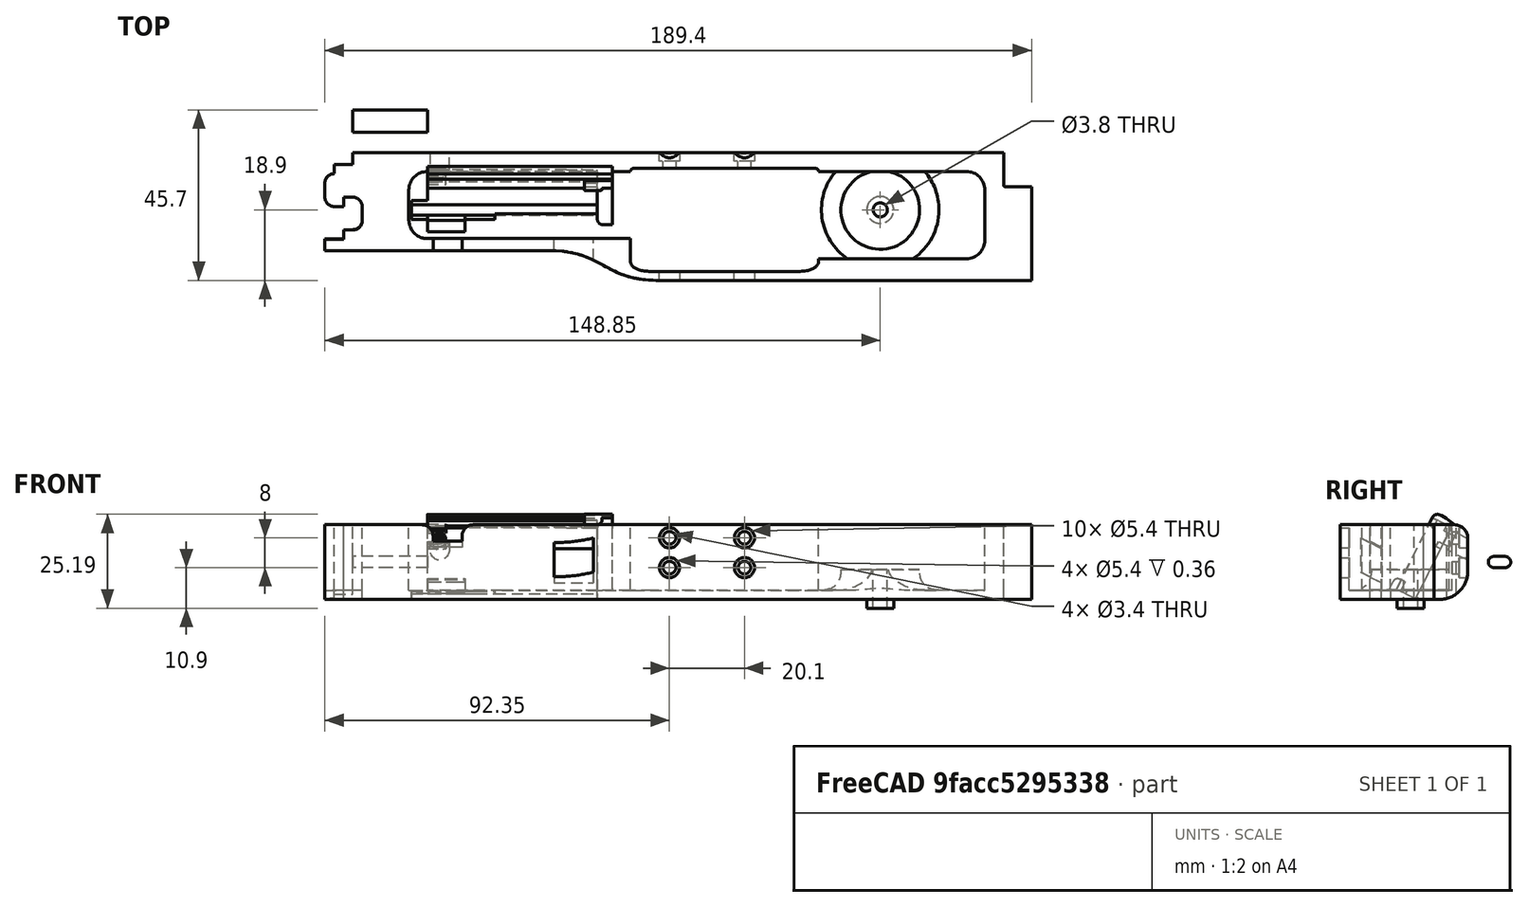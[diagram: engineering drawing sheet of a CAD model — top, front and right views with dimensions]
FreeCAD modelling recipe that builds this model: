
FCSTD DOCUMENT  (FreeCAD 0.19R0.19.2)
Label: v0_994
License: All rights reserved
LicenseURL: http://en.wikipedia.org/wiki/All_rights_reserved
objects: Sketcher::SketchObject×37, Part::Extrusion×31, Part::MultiFuse×17, Part::Cut×14, Part::Fillet×13, Part::Box×12, App::MeasureDistance×4, Part::Cylinder×4, Part::Revolution×1, Mesh::Feature×1
note: 129 computed .brp shape members not serialized (recipe doc carries the construction recipe); baked Part::Feature solids carry a one-line shape summary decoded from their .brp

FEATURE [Sketcher::SketchObject] Sketch
  FullyConstrained = true
  sketch-geometry (36):
    g0: LineSegment StartX=0 StartY=0 StartZ=0 EndX=154.4 EndY=0 EndZ=0
    g1: LineSegment StartX=154.4 StartY=0 StartZ=0 EndX=154.4 EndY=-7.6 EndZ=0
    g2: LineSegment StartX=32.5209 StartY=-26.2 StartZ=0 EndX=-7.5 EndY=-26.2 EndZ=0
    g3-g7: Circle x5 (B-spline internal-alignment scaffolding for g8; pole/knot coordinates omitted)
    g8: BSplineCurve PolesCount=5 KnotsCount=3 Degree=3 IsPeriodic=0
    g9: GeomPoint X=61.85 Y=-33.8 Z=0
    g10: GeomPoint X=47.185 Y=-29.9 Z=0
    g11: GeomPoint X=32.5209 Y=-26.2 Z=0
    g12: Circle CenterX=121.35 CenterY=-14.3 CenterZ=0 NormalX=0 NormalY=0 NormalZ=1 AngleXU=0 Radius=3.25
    g13: LineSegment StartX=-7.5 StartY=-26.2 StartZ=0 EndX=-27.5 EndY=-26.2 EndZ=0
    g14: LineSegment StartX=-20 StartY=0 StartZ=0 EndX=0 EndY=0 EndZ=0
    g15: LineSegment StartX=-25 StartY=-3.1 StartZ=0 EndX=-20 EndY=-3.1 EndZ=0
    g16: LineSegment StartX=-25 StartY=-3.1 StartZ=0 EndX=-25 EndY=-5.6 EndZ=0
    g17: LineSegment StartX=-27.5 StartY=-8.1 StartZ=0 EndX=-27.5 EndY=-11.85 EndZ=0
    g18: ArcOfCircle CenterX=-25 CenterY=-8.1 CenterZ=0 NormalX=0 NormalY=0 NormalZ=1 AngleXU=0 Radius=2.5 StartAngle=1.5708 EndAngle=3.14159
    g19: LineSegment StartX=-25 StartY=-14.35 StartZ=0 EndX=-22.5 EndY=-14.35 EndZ=0
    g20: ArcOfCircle CenterX=-25 CenterY=-11.85 CenterZ=0 NormalX=0 NormalY=0 NormalZ=1 AngleXU=0 Radius=2.5 StartAngle=3.14159 EndAngle=4.71239
    g21: LineSegment StartX=-22.5 StartY=-14.35 StartZ=0 EndX=-22.5 EndY=-11.85 EndZ=0
    g22: LineSegment StartX=-22.5 StartY=-11.85 StartZ=0 EndX=-20 EndY=-11.85 EndZ=0
    g23: ArcOfCircle CenterX=-20 CenterY=-14.35 CenterZ=0 NormalX=0 NormalY=0 NormalZ=1 AngleXU=0 Radius=2.5 StartAngle=8e-16 EndAngle=1.5708
    g24: LineSegment StartX=-17.5 StartY=-14.35 StartZ=0 EndX=-17.5 EndY=-18.1 EndZ=0
    g25: ArcOfCircle CenterX=-20 CenterY=-18.1 CenterZ=0 NormalX=0 NormalY=0 NormalZ=1 AngleXU=0 Radius=2.5 StartAngle=4.71239 EndAngle=6.28319
    g26: LineSegment StartX=-22.5 StartY=-20.6 StartZ=0 EndX=-20 EndY=-20.6 EndZ=0
    g27: LineSegment StartX=-22.5 StartY=-20.6 StartZ=0 EndX=-22.5 EndY=-23.1 EndZ=0
    g28: LineSegment StartX=-27.5 StartY=-23.1 StartZ=0 EndX=-22.5 EndY=-23.1 EndZ=0
    g29: LineSegment StartX=-20 StartY=-3.1 StartZ=0 EndX=-20 EndY=0 EndZ=0
    g30: LineSegment StartX=-27.5 StartY=-23.1 StartZ=0 EndX=-27.5 EndY=-26.2 EndZ=0
    g31: LineSegment StartX=154.4 StartY=-7.6 StartZ=0 EndX=154.4 EndY=-8.6 EndZ=0
    g32: ArcOfCircle CenterX=154.9 CenterY=-8.6 CenterZ=0 NormalX=0 NormalY=0 NormalZ=1 AngleXU=0 Radius=0.5 StartAngle=3.14159 EndAngle=4.71239
    g33: LineSegment StartX=154.9 StartY=-9.1 StartZ=0 EndX=161.9 EndY=-9.1 EndZ=0
    g34: LineSegment StartX=161.9 StartY=-9.1 StartZ=0 EndX=161.9 EndY=-33.8 EndZ=0
    g35: LineSegment StartX=161.9 StartY=-33.8 StartZ=0 EndX=61.85 EndY=-33.8 EndZ=0
  constraints (72):
    c: PointOnObject(g0,g-2)
    c: Horizontal(g0)
    c: Distance(g0) = 154.4
    c: DistanceY(g-1,g0) = 0
    c: Vertical(g1)
    c: Distance(g1) = 7.6
    c: Coincident(g1,g0)
    c: Horizontal(g2)
    c: Block(g2)
    c: Weight(g3) = 1
    c: Coincident(g8,g2)
    c: InternalAlignment(g3-g7 -> g8) x5
    c: InternalAlignment(g9,g8)
    c: InternalAlignment(g10,g8)
    c: InternalAlignment(g11,g8)
    c: Block(g12)
    c: Coincident(g13,g2)
    c: Horizontal(g13)
    c: Distance(g13) = 20
    c: Horizontal(g14)
    c: Distance(g14) = 20
    c: Coincident(g14,g0)
    c: Horizontal(g15)
    c: Vertical(g16)
    c: Coincident(g16,g15)
    c: Vertical(g17)
    c: Coincident(g18,g16)
    c: Block(g18)
    c: Coincident(g17,g18)
    c: Horizontal(g19)
    c: Coincident(g20,g17)
    c: Block(g20)
    c: Block(g19)
    c: Vertical(g21)
    c: Coincident(g21,g19)
    c: Horizontal(g22)
    c: Coincident(g22,g21)
    c: Coincident(g23,g22)
    c: Vertical(g24)
    c: Block(g23)
    c: Coincident(g24,g23)
    c: Coincident(g25,g24)
    c: Block(g25)
    c: Horizontal(g26)
    c: Coincident(g26,g25)
    c: Vertical(g27)
    c: Coincident(g27,g26)
    c: Horizontal(g28)
    c: Coincident(g28,g27)
    c: Block(g15)
    c: Block(g28)
    c: Coincident(g29,g15)
    c: Coincident(g29,g14)
    c: Vertical(g29)
    c: Coincident(g30,g28)
    c: Coincident(g30,g13)
    c: Vertical(g30)
    c: Vertical(g31)
    c: Distance(g31) = 1
    c: Coincident(g31,g1)
    c: Coincident(g32,g31)
    c: Block(g32)
    c: Coincident(g33,g32)
    c: Horizontal(g33)
    c: Coincident(g34,g33)
    c: Vertical(g34)
    c: Block(g34)
    c: Coincident(g35,g34)
    c: Horizontal(g35)
    c: Block(g35)
    c: Coincident(g8,g35)
    c: Block(g8)
FEATURE [Part::Extrusion] Extrude  label="mainBodyBaseExtrude"
  Base = -> Sketch
  Dir = (0,0,1)
  DirMode = 2
  FaceMakerClass = Part::FaceMakerBullseye
  LengthFwd = 2.4
  LengthRev = 0
  Solid = true
  Symmetric = false
FEATURE [Sketcher::SketchObject] Sketch001
  FullyConstrained = true
  sketch-geometry (75):
    g0: ArcOfCircle CenterX=144.4 CenterY=-10 CenterZ=0 NormalX=0 NormalY=0 NormalZ=1 AngleXU=0 Radius=5 StartAngle=4.345e-13 EndAngle=1.5708
    g1: LineSegment StartX=32.5209 StartY=-26.2 StartZ=0 EndX=-7.49911 EndY=-26.2 EndZ=0
    g2: LineSegment StartX=0 StartY=0 StartZ=0 EndX=154.4 EndY=0 EndZ=0
    g3-g7: Circle x5 (B-spline internal-alignment scaffolding for g8; pole/knot coordinates omitted)
    g8: BSplineCurve PolesCount=5 KnotsCount=3 Degree=3 IsPeriodic=0
    g9: GeomPoint X=61.85 Y=-33.8 Z=0
    g10: GeomPoint X=47.1857 Y=-29.9 Z=0
    g11: GeomPoint X=32.5209 Y=-26.2 Z=0
    g12: LineSegment StartX=154.4 StartY=0 StartZ=0 EndX=154.4 EndY=-7.6 EndZ=0
    g13: LineSegment StartX=20 StartY=-5 StartZ=0 EndX=54.35 EndY=-5 EndZ=0
    g14: LineSegment StartX=104.85 StartY=-5 StartZ=0 EndX=144.4 EndY=-5 EndZ=0
    g15: LineSegment StartX=54.35 StartY=-23 StartZ=0 EndX=20 EndY=-23 EndZ=0
    g16: LineSegment StartX=-27.4991 StartY=-26.2 StartZ=0 EndX=-7.49911 EndY=-26.2 EndZ=0
    g17: LineSegment StartX=-20 StartY=0 StartZ=0 EndX=0 EndY=0 EndZ=0
    g18: LineSegment StartX=-27.4991 StartY=-23.2 StartZ=0 EndX=-22.5 EndY=-23.2 EndZ=0
    g19: LineSegment StartX=-22.5 StartY=-20.7 StartZ=0 EndX=-22.5 EndY=-23.2 EndZ=0
    g20: LineSegment StartX=-22.5 StartY=-20.7 StartZ=0 EndX=-20 EndY=-20.7 EndZ=0
    g21: ArcOfCircle CenterX=-20 CenterY=-18.2 CenterZ=0 NormalX=0 NormalY=0 NormalZ=1 AngleXU=0 Radius=2.5 StartAngle=4.71239 EndAngle=6.28319
    g22: LineSegment StartX=-17.5 StartY=-14.4 StartZ=0 EndX=-17.5 EndY=-18.2 EndZ=0
    g23: ArcOfCircle CenterX=-20 CenterY=-14.4 CenterZ=0 NormalX=0 NormalY=0 NormalZ=1 AngleXU=0 Radius=2.5 StartAngle=9e-16 EndAngle=1.5708
    g24: LineSegment StartX=-22.5 StartY=-11.9 StartZ=0 EndX=-20 EndY=-11.9 EndZ=0
    g25: LineSegment StartX=-22.5 StartY=-14.4 StartZ=0 EndX=-22.5 EndY=-11.9 EndZ=0
    g26: LineSegment StartX=-25 StartY=-14.4 StartZ=0 EndX=-22.5 EndY=-14.4 EndZ=0
    g27: ArcOfCircle CenterX=-25 CenterY=-11.9 CenterZ=0 NormalX=0 NormalY=0 NormalZ=1 AngleXU=0 Radius=2.5 StartAngle=3.14159 EndAngle=4.71239
    g28: LineSegment StartX=-27.5 StartY=-8.1 StartZ=0 EndX=-27.5 EndY=-11.9 EndZ=0
    g29: ArcOfCircle CenterX=-25 CenterY=-8.1 CenterZ=0 NormalX=0 NormalY=0 NormalZ=1 AngleXU=0 Radius=2.5 StartAngle=1.5708 EndAngle=3.14159
    g30: LineSegment StartX=-25 StartY=-3.1 StartZ=0 EndX=-25 EndY=-5.6 EndZ=0
    g31: LineSegment StartX=-20 StartY=-3.1 StartZ=0 EndX=-25 EndY=-3.1 EndZ=0
    g32: LineSegment StartX=-20 StartY=0 StartZ=0 EndX=-20 EndY=-3.1 EndZ=0
    g33: LineSegment StartX=-27.4991 StartY=-26.2 StartZ=0 EndX=-27.4991 EndY=-23.2 EndZ=0
    g34: LineSegment StartX=4.09e-14 StartY=-5 StartZ=0 EndX=20 EndY=-5 EndZ=0
    g35: ArcOfCircle CenterX=7.1e-15 CenterY=-18 CenterZ=0 NormalX=0 NormalY=0 NormalZ=1 AngleXU=0 Radius=5 StartAngle=3.14159 EndAngle=4.71239
    g36: ArcOfCircle CenterX=4.26e-14 CenterY=-10 CenterZ=0 NormalX=0 NormalY=0 NormalZ=1 AngleXU=0 Radius=5 StartAngle=1.5708 EndAngle=3.14159
    g37: LineSegment StartX=-5 StartY=-18 StartZ=0 EndX=-5 EndY=-10 EndZ=0
    g38: LineSegment StartX=6.2e-15 StartY=-23 StartZ=0 EndX=20 EndY=-23 EndZ=0
    g39: LineSegment StartX=154.4 StartY=-7.6 StartZ=0 EndX=154.4 EndY=-8.6 EndZ=0
    g40: LineSegment StartX=154.9 StartY=-9.1 StartZ=0 EndX=161.9 EndY=-9.1 EndZ=0
    g41: ArcOfCircle CenterX=154.9 CenterY=-8.6 CenterZ=0 NormalX=0 NormalY=0 NormalZ=1 AngleXU=0 Radius=0.5 StartAngle=3.14159 EndAngle=4.71299
    g42: LineSegment StartX=104.85 StartY=-28.3916 StartZ=0 EndX=144.408 EndY=-28.3916 EndZ=0
    g43: LineSegment StartX=149.4 StartY=-10 StartZ=0 EndX=149.4 EndY=-23.4 EndZ=0
    g44: ArcOfCircle CenterX=144.408 CenterY=-23.4 CenterZ=0 NormalX=0 NormalY=0 NormalZ=1 AngleXU=0 Radius=4.99164 StartAngle=4.71239 EndAngle=6.28319
    g45: LineSegment StartX=104.85 StartY=-28.3916 StartZ=0 EndX=104.85 EndY=-28.7833 EndZ=0
    g46: LineSegment StartX=54.35 StartY=-28.7916 StartZ=0 EndX=54.35 EndY=-23 EndZ=0
    g47: LineSegment StartX=161.9 StartY=-33.8 StartZ=0 EndX=161.9 EndY=-9.1 EndZ=0
    g48: LineSegment StartX=61.85 StartY=-33.8 StartZ=0 EndX=161.9 EndY=-33.8 EndZ=0
    g49: Circle CenterX=54.35 CenterY=-28.7916 CenterZ=0 NormalX=0 NormalY=0 NormalZ=1 AngleXU=0 Radius=1
    g50: Circle CenterX=54.35 CenterY=-31.7916 CenterZ=0 NormalX=0 NormalY=0 NormalZ=1 AngleXU=0 Radius=1
    g51: Circle CenterX=57.35 CenterY=-31.7916 CenterZ=0 NormalX=0 NormalY=0 NormalZ=1 AngleXU=0 Radius=1
    g52: BSplineCurve PolesCount=3 KnotsCount=2 Degree=2 IsPeriodic=0
    g53: GeomPoint X=54.35 Y=-28.7916 Z=0
    g54: GeomPoint X=57.35 Y=-31.7916 Z=0
    g55: Circle CenterX=104.85 CenterY=-28.7833 CenterZ=0 NormalX=0 NormalY=0 NormalZ=1 AngleXU=0 Radius=1
    g56: Circle CenterX=104.85 CenterY=-31.7916 CenterZ=0 NormalX=0 NormalY=0 NormalZ=1 AngleXU=0 Radius=1
    g57: Circle CenterX=101.85 CenterY=-31.7916 CenterZ=0 NormalX=0 NormalY=0 NormalZ=1 AngleXU=0 Radius=1
    g58: BSplineCurve PolesCount=3 KnotsCount=2 Degree=2 IsPeriodic=0
    g59: GeomPoint X=104.85 Y=-28.7833 Z=0
    g60: GeomPoint X=101.85 Y=-31.7916 Z=0
    g61: LineSegment StartX=57.35 StartY=-31.7916 StartZ=0 EndX=101.85 EndY=-31.7916 EndZ=0
    g62: Circle CenterX=54.35 CenterY=-5 CenterZ=0 NormalX=0 NormalY=0 NormalZ=1 AngleXU=0 Radius=1
    g63: Circle CenterX=54.35 CenterY=-4 CenterZ=0 NormalX=0 NormalY=0 NormalZ=1 AngleXU=0 Radius=1
    g64: Circle CenterX=55.15 CenterY=-4 CenterZ=0 NormalX=0 NormalY=0 NormalZ=1 AngleXU=0 Radius=1
    g65: BSplineCurve PolesCount=3 KnotsCount=2 Degree=2 IsPeriodic=0
    g66: GeomPoint X=54.35 Y=-5 Z=0
    g67: GeomPoint X=55.15 Y=-4 Z=0
    g68: Circle CenterX=104.85 CenterY=-5 CenterZ=0 NormalX=0 NormalY=0 NormalZ=1 AngleXU=0 Radius=1
    g69: Circle CenterX=104.85 CenterY=-4 CenterZ=0 NormalX=0 NormalY=0 NormalZ=1 AngleXU=0 Radius=1
    g70: Circle CenterX=104.05 CenterY=-4 CenterZ=0 NormalX=0 NormalY=0 NormalZ=1 AngleXU=0 Radius=1
    g71: BSplineCurve PolesCount=3 KnotsCount=2 Degree=2 IsPeriodic=0
    g72: GeomPoint X=104.85 Y=-5 Z=0
    g73: GeomPoint X=104.05 Y=-4 Z=0
    g74: LineSegment StartX=104.05 StartY=-4 StartZ=0 EndX=55.15 EndY=-4 EndZ=0
  constraints (156):
    c: PointOnObject(g2,g-2)
    c: DistanceY(g-1,g2) = 0
    c: Block(g0)
    c: Horizontal(g1)
    c: Distance(g1) = 40.02
    c: Horizontal(g2)
    c: Block(g2)
    c: Weight(g3) = 1
    c: Equal(g3, g4-g7) x4
    c: Coincident(g8,g1)
    c: InternalAlignment(g3-g7 -> g8) x5
    c: InternalAlignment(g9,g8)
    c: InternalAlignment(g10,g8)
    c: InternalAlignment(g11,g8)
    c: Vertical(g12)
    c: Coincident(g12,g2)
    c: Distance(g12) = 7.6
    c: Block(g12)
    c: Horizontal(g13)
    c: Coincident(g14,g0)
    c: Horizontal(g14)
    c: Horizontal(g15)
    c: Horizontal(g16)
    c: Distance(g16) = 20
    c: Coincident(g1,g16)
    c: Horizontal(g17)
    c: Distance(g17) = 20
    c: Coincident(g17,g2)
    c: Horizontal(g31)
    c: Vertical(g30)
    c: Coincident(g29,g30)
    c: Vertical(g28)
    c: Block(g29)
    c: Coincident(g27,g28)
    c: Block(g27)
    c: Horizontal(g26)
    c: Coincident(g26,g27)
    c: Vertical(g25)
    c: Coincident(g25,g26)
    c: Horizontal(g24)
    c: Coincident(g23,g24)
    c: Block(g23)
    c: Vertical(g22)
    c: Coincident(g21,g22)
    c: Block(g21)
    c: Horizontal(g20)
    c: Coincident(g20,g21)
    c: Vertical(g19)
    c: Coincident(g19,g20)
    c: Horizontal(g18)
    c: Coincident(g18,g19)
    c: Coincident(g32,g17)
    c: Coincident(g32,g31)
    c: Vertical(g32)
    c: Coincident(g33,g16)
    c: Coincident(g33,g18)
    c: Vertical(g33)
    c: Block(g33)
    c: Block(g18)
    c: Block(g22)
    c: Block(g26)
    c: Block(g25)
    c: Block(g24)
    c: Block(g28)
    c: Block(g31)
    c: Block(g30)
    c: Horizontal(g34)
    c: Distance(g34) = 20
    c: Block(g35)
    c: Block(g36)
    c: Coincident(g37,g35)
    c: Coincident(g37,g36)
    c: Vertical(g37)
    c: Coincident(g38,g35)
    c: Coincident(g38,g15)
    c: Horizontal(g38)
    c: Block(g38)
    c: Block(g34)
    c: Block(g13)
    c: Vertical(g39)
    c: Distance(g39) = 1
    c: Coincident(g39,g12)
    c: Horizontal(g40)
    c: Coincident(g41,g39)
    c: Coincident(g41,g40)
    c: Block(g39)
    c: Block(g41)
    c: Horizontal(g42)
    c: Vertical(g43)
    c: Distance(g43) = 13.4
    c: Coincident(g43,g0)
    c: Block(g42)
    c: Block(g43)
    c: Coincident(g44,g43)
    c: Coincident(g44,g42)
    c: Block(g44)
    c: Distance(g15) = 34.35
    c: Coincident(g45,g42)
    c: Vertical(g45)
    c: Coincident(g46,g15)
    c: Vertical(g46)
    c: Coincident(g47,g40)
    c: Vertical(g47)
    c: Block(g47)
    c: Coincident(g48,g47)
    c: Horizontal(g48)
    c: Block(g48)
    c: Coincident(g8,g48)
    c: Block(g8)
    c: Coincident(g52,g46)
    c: Weight(g49) = 1
    c: Equal(g49,g50)
    c: Equal(g49,g51)
    c: InternalAlignment(g49,g52)
    c: InternalAlignment(g50,g52)
    c: InternalAlignment(g51,g52)
    c: InternalAlignment(g53,g52)
    c: InternalAlignment(g54,g52)
    c: Coincident(g58,g45)
    c: Weight(g55) = 1
    c: Equal(g55,g56)
    c: Equal(g55,g57)
    c: InternalAlignment(g55,g58)
    c: InternalAlignment(g56,g58)
    c: InternalAlignment(g57,g58)
    c: InternalAlignment(g59,g58)
    c: InternalAlignment(g60,g58)
    c: Block(g58)
    c: Block(g52)
    c: Coincident(g61,g52)
    c: Coincident(g61,g58)
    c: Horizontal(g61)
    c: Block(g14)
    c: Coincident(g65,g13)
    c: Weight(g62) = 1
    c: Equal(g62,g63)
    c: Equal(g62,g64)
    c: InternalAlignment(g62,g65)
    c: InternalAlignment(g63,g65)
    c: InternalAlignment(g64,g65)
    c: InternalAlignment(g66,g65)
    c: InternalAlignment(g67,g65)
    c: Block(g65)
    c: Coincident(g71,g14)
    c: Weight(g68) = 1
    c: Equal(g68,g69)
    c: Equal(g68,g70)
    c: InternalAlignment(g68,g71)
    c: InternalAlignment(g69,g71)
    c: InternalAlignment(g70,g71)
    c: InternalAlignment(g72,g71)
    c: InternalAlignment(g73,g71)
    c: Block(g71)
    c: Coincident(g74,g71)
    c: Coincident(g74,g65)
    c: Horizontal(g74)
FEATURE [Sketcher::SketchObject] Sketch005
  FullyConstrained = true
  Placement = pos=(0,0,0) rot=(1,0,0;1.5708rad)
  sketch-geometry (4):
    g0: Circle CenterX=84.95 CenterY=16.5 CenterZ=0 NormalX=0 NormalY=0 NormalZ=1 AngleXU=0 Radius=1.7
    g1: Circle CenterX=84.95 CenterY=8.5 CenterZ=0 NormalX=0 NormalY=0 NormalZ=1 AngleXU=0 Radius=1.7
    g2: Circle CenterX=64.85 CenterY=8.5 CenterZ=0 NormalX=0 NormalY=0 NormalZ=1 AngleXU=0 Radius=1.7
    g3: Circle CenterX=64.85 CenterY=16.5 CenterZ=0 NormalX=0 NormalY=0 NormalZ=1 AngleXU=0 Radius=1.7
  constraints (4):
    c: Block(g0)
    c: Block(g1)
    c: Block(g2)
    c: Block(g3)
FEATURE [Part::Extrusion] Extrude004  label="removeFromMainBodyToCreateScrewHolesForSolenoidExtrude004"
  Base = -> Sketch005
  Dir = (0,-1,1.1e-15)
  DirMode = 2
  FaceMakerClass = Part::FaceMakerBullseye
  LengthFwd = 10
  LengthRev = 0
  Solid = true
  Symmetric = false
FEATURE [Sketcher::SketchObject] Sketch004
  FullyConstrained = true
  Placement = pos=(0,0,0) rot=(1,0,0;1.5708rad)
  sketch-geometry (12):
    g0: LineSegment StartX=15.75 StartY=2.5 StartZ=0 EndX=15.75 EndY=0 EndZ=0
    g1: Circle CenterX=15.75 CenterY=2.5 CenterZ=0 NormalX=0 NormalY=0 NormalZ=1 AngleXU=0 Radius=1
    g2: Circle CenterX=10.55 CenterY=2.5 CenterZ=0 NormalX=0 NormalY=0 NormalZ=1 AngleXU=0 Radius=1
    g3: Circle CenterX=10.55 CenterY=8 CenterZ=0 NormalX=0 NormalY=0 NormalZ=1 AngleXU=0 Radius=1
    g4: BSplineCurve PolesCount=3 KnotsCount=2 Degree=2 IsPeriodic=0
    g5: GeomPoint X=15.75 Y=2.5 Z=0
    g6: GeomPoint X=10.55 Y=8 Z=0
    g7: LineSegment StartX=1.9 StartY=8 StartZ=0 EndX=10.55 EndY=8 EndZ=0
    g8: LineSegment StartX=1.9 StartY=-2.4 StartZ=0 EndX=1.9 EndY=8 EndZ=0
    g9: LineSegment StartX=3.30092 StartY=-2.4 StartZ=0 EndX=3.30092 EndY=0 EndZ=0
    g10: LineSegment StartX=15.75 StartY=0 StartZ=0 EndX=3.30092 EndY=0 EndZ=0
    g11: LineSegment StartX=3.30092 StartY=-2.4 StartZ=0 EndX=1.9 EndY=-2.4 EndZ=0
  constraints (26):
    c: Vertical(g0)
    c: Distance(g0) = 2.5
    c: Coincident(g4,g0)
    c: Weight(g1) = 1
    c: Equal(g1,g2)
    c: Equal(g1,g3)
    c: InternalAlignment(g1,g4)
    c: InternalAlignment(g2,g4)
    c: InternalAlignment(g3,g4)
    c: InternalAlignment(g5,g4)
    c: InternalAlignment(g6,g4)
    c: Block(g4)
    c: Coincident(g7,g4)
    c: Horizontal(g7)
    c: Vertical(g8)
    c: Coincident(g8,g7)
    c: Block(g8)
    c: Vertical(g9)
    c: Coincident(g10,g0)
    c: PointOnObject(g10,g-1)
    c: Horizontal(g10)
    c: Coincident(g10,g9)
    c: Block(g9)
    c: Coincident(g11,g9)
    c: Coincident(g11,g8)
    c: Horizontal(g11)
FEATURE [Sketcher::SketchObject] Sketch007
  FullyConstrained = true
  Placement = pos=(0,-14.3,2.37) rot=(-1,0,0;2.03453rad)
  sketch-geometry (6):
    g0: LineSegment StartX=0 StartY=0 StartZ=0 EndX=45.5 EndY=0 EndZ=0
    g1: LineSegment StartX=0 StartY=0 StartZ=0 EndX=0 EndY=-21.2 EndZ=0
    g2: LineSegment StartX=45.5 StartY=0 StartZ=0 EndX=49.5 EndY=0 EndZ=0
    g3: LineSegment StartX=49.5 StartY=0 StartZ=0 EndX=49.5 EndY=-21.2 EndZ=0
    g4: LineSegment StartX=49.5 StartY=-21.2 StartZ=0 EndX=0 EndY=-21.2 EndZ=0
    g5: Circle CenterX=3.25 CenterY=-18.05 CenterZ=0 NormalX=0 NormalY=0 NormalZ=1 AngleXU=0 Radius=1.6
  constraints (15):
    c: Coincident(g0,g-1)
    c: Horizontal(g0)
    c: Distance(g0) = 45.5
    c: Coincident(g1,g0)
    c: Vertical(g1)
    c: Horizontal(g2)
    c: Distance(g2) = 4
    c: Coincident(g2,g0)
    c: Coincident(g3,g2)
    c: Vertical(g3)
    c: Block(g3)
    c: Coincident(g4,g3)
    c: Horizontal(g4)
    c: Coincident(g4,g1)
    c: Block(g5)
FEATURE [Part::Extrusion] Extrude005  label="solenoidDriverHolderExtrude005"
  Base = -> Sketch007
  Dir = (0,0.894389,-0.447291)
  DirMode = 2
  FaceMakerClass = Part::FaceMakerBullseye
  LengthFwd = 10
  LengthRev = 0
  Placement = pos=(0,0,-2) rot=(0,0,1;0rad)
  Solid = true
  Symmetric = false
FEATURE [Sketcher::SketchObject] Sketch008
  FullyConstrained = false
  Placement = pos=(0,-4.3,-2.6) rot=(-1,0,0;2.03453rad)
  sketch-geometry (1):
    g0: Circle CenterX=42.25 CenterY=-3.15 CenterZ=0 NormalX=0 NormalY=0 NormalZ=1 AngleXU=0 Radius=4.5
FEATURE [Sketcher::SketchObject] Sketch009
  FullyConstrained = true
  Placement = pos=(0,-4.3,-2.6) rot=(-1,0,0;2.03453rad)
  sketch-geometry (1):
    g0: Circle CenterX=3.25 CenterY=-18.0217 CenterZ=0 NormalX=0 NormalY=0 NormalZ=1 AngleXU=0 Radius=2.8
  constraints (1):
    c: Block(g0)
FEATURE [Sketcher::SketchObject] Sketch010
  FullyConstrained = true
  Placement = pos=(0,-14.3,2.37) rot=(-1,0,0;2.03453rad)
  sketch-geometry (1):
    g0: Circle CenterX=3.25 CenterY=-18.05 CenterZ=0 NormalX=0 NormalY=0 NormalZ=1 AngleXU=0 Radius=1.6
  constraints (1):
    c: Block(g0)
FEATURE [Part::Extrusion] Extrude008  label="removeFromScrewHole3"
  Base = -> Sketch010
  Dir = (0,0.894389,-0.447291)
  DirMode = 2
  FaceMakerClass = Part::FaceMakerBullseye
  LengthFwd = -25
  LengthRev = 0
  Placement = pos=(0,4,-4) rot=(0,0,1;0rad)
  Solid = true
  Symmetric = false
FEATURE [Sketcher::SketchObject] Sketch011
  FullyConstrained = true
  Placement = pos=(0,-14.3,2.37) rot=(-1,0,0;2.03453rad)
  sketch-geometry (4):
    g0: LineSegment StartX=49.5 StartY=-21.2 StartZ=0 EndX=49.5 EndY=-22.8 EndZ=0
    g1: LineSegment StartX=49.5 StartY=-22.8 StartZ=0 EndX=0.002238 EndY=-22.8 EndZ=0
    g2: LineSegment StartX=0.002238 StartY=-21.2 StartZ=0 EndX=0.002238 EndY=-22.8 EndZ=0
    g3: LineSegment StartX=49.5 StartY=-21.2 StartZ=0 EndX=0.002238 EndY=-21.2 EndZ=0
  constraints (10):
    c: Vertical(g0)
    c: Distance(g0) = 1.6
    c: Coincident(g1,g0)
    c: Horizontal(g1)
    c: Vertical(g2)
    c: Coincident(g2,g1)
    c: Coincident(g3,g0)
    c: Coincident(g3,g2)
    c: Horizontal(g3)
    c: Block(g3)
FEATURE [Part::Extrusion] Extrude009  label="solenoidDriverTopLipFront"
  Base = -> Sketch011
  Dir = (0,0.894389,-0.447291)
  DirMode = 2
  FaceMakerClass = Part::FaceMakerBullseye
  LengthFwd = -2
  LengthRev = 0
  Placement = pos=(0,-2.9,-0.35) rot=(0,0,1;0rad)
  Solid = true
  Symmetric = false
FEATURE [Sketcher::SketchObject] Sketch012
  FullyConstrained = true
  Placement = pos=(0,-14.3,2.37) rot=(-1,0,0;2.03453rad)
  sketch-geometry (4):
    g0: LineSegment StartX=49.5 StartY=-21.2 StartZ=0 EndX=49.5 EndY=-22.8 EndZ=0
    g1: LineSegment StartX=49.5 StartY=-22.8 StartZ=0 EndX=0.002238 EndY=-22.8 EndZ=0
    g2: LineSegment StartX=0.002238 StartY=-21.2 StartZ=0 EndX=0.002238 EndY=-22.8 EndZ=0
    g3: LineSegment StartX=49.5 StartY=-21.2 StartZ=0 EndX=0.002238 EndY=-21.2 EndZ=0
  constraints (10):
    c: Vertical(g0)
    c: Distance(g0) = 1.6
    c: Coincident(g1,g0)
    c: Horizontal(g1)
    c: Vertical(g2)
    c: Coincident(g2,g1)
    c: Coincident(g3,g0)
    c: Coincident(g3,g2)
    c: Horizontal(g3)
    c: Block(g3)
FEATURE [Part::Extrusion] Extrude010  label="solenoidDriverTopLipLowerExtrude010"
  Base = -> Sketch012
  Dir = (0,0.894389,-0.447291)
  DirMode = 2
  FaceMakerClass = Part::FaceMakerBullseye
  LengthFwd = 5.05
  LengthRev = 0
  Solid = true
  Symmetric = false
FEATURE [Sketcher::SketchObject] Sketch015
  FullyConstrained = true
  Placement = pos=(0,-14.3,2.37) rot=(-1,0,0;2.03453rad)
  sketch-geometry (4):
    g0: LineSegment StartX=0 StartY=1.5 StartZ=0 EndX=0 EndY=0 EndZ=0
    g1: LineSegment StartX=0 StartY=1.5 StartZ=0 EndX=5 EndY=1.5 EndZ=0
    g2: LineSegment StartX=5 StartY=1.5 StartZ=0 EndX=5 EndY=0 EndZ=0
    g3: LineSegment StartX=0 StartY=0 StartZ=0 EndX=5 EndY=0 EndZ=0
  constraints (13):
    c: Vertical(g0)
    c: Distance(g0) = 1.5
    c: Horizontal(g1)
    c: Distance(g1) = 5
    c: Coincident(g1,g0)
    c: Vertical(g2)
    c: Distance(g2) = 1.5
    c: Coincident(g2,g1)
    c: Block(g1)
    c: Block(g2)
    c: Block(g0)
    c: Coincident(g3,g0)
    c: Coincident(g3,g2)
FEATURE [Part::Extrusion] Extrude013  label="solenoidDriverBottomLipTopExtrude012"
  Base = -> Sketch015
  Dir = (0,0.894389,-0.447291)
  DirMode = 2
  FaceMakerClass = Part::FaceMakerBullseye
  LengthFwd = -6.5
  LengthRev = 0
  Placement = pos=(0,-14.15,19.65) rot=(1,0,0;1.5708rad)
  Solid = true
  Symmetric = false
FEATURE [Sketcher::SketchObject] Sketch016
  FullyConstrained = true
  Placement = pos=(0,0,0) rot=(1,0,0;1.5708rad)
  sketch-geometry (4):
    g0: Circle CenterX=84.15 CenterY=16.5 CenterZ=0 NormalX=0 NormalY=0 NormalZ=1 AngleXU=0 Radius=2.7
    g1: Circle CenterX=64.05 CenterY=16.5 CenterZ=0 NormalX=0 NormalY=0 NormalZ=1 AngleXU=0 Radius=2.7
    g2: Circle CenterX=64.05 CenterY=8.5 CenterZ=0 NormalX=0 NormalY=0 NormalZ=1 AngleXU=0 Radius=2.7
    g3: Circle CenterX=84.15 CenterY=8.5 CenterZ=0 NormalX=0 NormalY=0 NormalZ=1 AngleXU=0 Radius=2.7
  constraints (4):
    c: Block(g0)
    c: Block(g1)
    c: Block(g3)
    c: Block(g2)
FEATURE [Part::Extrusion] Extrude014  label="removeFromMainBodyToCreateScrewHoleCounterSinks"
  Base = -> Sketch016
  Dir = (0,-1,1.1e-15)
  DirMode = 2
  FaceMakerClass = Part::FaceMakerBullseye
  LengthFwd = 1.9
  LengthRev = 0
  Placement = pos=(0.8,-0.36,0) rot=(0,0,1;0rad)
  Solid = true
  Symmetric = false
FEATURE [Part::Extrusion] Extrude015  label="removeFromScrewHole2Extrude007"
  Base = -> Sketch009
  Dir = (0,0.894389,-0.447291)
  DirMode = 2
  FaceMakerClass = Part::FaceMakerBullseye
  LengthFwd = 10
  LengthRev = 0
  Placement = pos=(0,-8,2) rot=(0,0,1;0rad)
  Solid = true
  Symmetric = false
FEATURE [Sketcher::SketchObject] Sketch017
  FullyConstrained = true
  Placement = pos=(0,-14.3,2.37) rot=(-1,0,0;2.03453rad)
  sketch-geometry (4):
    g0: LineSegment StartX=0 StartY=1.5 StartZ=0 EndX=0 EndY=0 EndZ=0
    g1: LineSegment StartX=0 StartY=1.5 StartZ=0 EndX=5 EndY=1.5 EndZ=0
    g2: LineSegment StartX=5 StartY=1.5 StartZ=0 EndX=5 EndY=0 EndZ=0
    g3: LineSegment StartX=0 StartY=0 StartZ=0 EndX=5 EndY=0 EndZ=0
  constraints (13):
    c: Vertical(g0)
    c: Distance(g0) = 1.5
    c: Horizontal(g1)
    c: Distance(g1) = 5
    c: Coincident(g1,g0)
    c: Vertical(g2)
    c: Distance(g2) = 1.5
    c: Coincident(g2,g1)
    c: Block(g1)
    c: Block(g2)
    c: Block(g0)
    c: Coincident(g3,g0)
    c: Coincident(g3,g2)
FEATURE [Part::Extrusion] Extrude016  label="solenoidDriverBottomLipTopExtrude013"
  Base = -> Sketch017
  Dir = (0,0.894389,-0.447291)
  DirMode = 2
  FaceMakerClass = Part::FaceMakerBullseye
  LengthFwd = -6.5
  LengthRev = 0
  Placement = pos=(0,-15.45,20.3) rot=(1,0,0;1.5708rad)
  Solid = true
  Symmetric = false
FEATURE [Part::Fillet] Fillet005  label="solenoidDriverBottomLipTopFillet005"
  Base = -> Extrude016
  Edges = 1 edges r=1.4: [Edge6]
FEATURE [Sketcher::SketchObject] Sketch018
  FullyConstrained = true
  Placement = pos=(38.5,-14.3,2.37) rot=(-1,0,0;2.03453rad)
  sketch-geometry (4):
    g0: LineSegment StartX=11 StartY=0 StartZ=0 EndX=11 EndY=1.5 EndZ=0
    g1: LineSegment StartX=11 StartY=0 StartZ=0 EndX=3.6 EndY=0 EndZ=0
    g2: LineSegment StartX=3.6 StartY=0 StartZ=0 EndX=3.6 EndY=1.5 EndZ=0
    g3: LineSegment StartX=11 StartY=1.5 StartZ=0 EndX=3.6 EndY=1.5 EndZ=0
  constraints (12):
    c: PointOnObject(g0,g-1)
    c: Vertical(g0)
    c: Distance(g0) = 1.5
    c: Horizontal(g1)
    c: Distance(g1) = 7.4
    c: Coincident(g1,g0)
    c: Block(g0)
    c: Coincident(g2,g1)
    c: Vertical(g2)
    c: Coincident(g3,g0)
    c: Horizontal(g3)
    c: Coincident(g2,g3)
FEATURE [Part::Extrusion] Extrude017
  Base = -> Sketch018
  Dir = (0,0.894389,-0.447291)
  DirMode = 2
  FaceMakerClass = Part::FaceMakerBullseye
  LengthFwd = 4
  LengthRev = 0
  Placement = pos=(0,-8.212,34.025) rot=(1,0,0;1.5708rad)
  Solid = true
  Symmetric = false
FEATURE [Sketcher::SketchObject] Sketch019
  FullyConstrained = true
  Placement = pos=(0,0,0) rot=(1,0,0;1.5708rad)
  sketch-geometry (4):
    g0: Circle CenterX=84.95 CenterY=8.5 CenterZ=0 NormalX=0 NormalY=0 NormalZ=1 AngleXU=0 Radius=2.7
    g1: Circle CenterX=64.85 CenterY=8.5 CenterZ=0 NormalX=0 NormalY=0 NormalZ=1 AngleXU=0 Radius=2.7
    g2: Circle CenterX=64.85 CenterY=16.5 CenterZ=0 NormalX=0 NormalY=0 NormalZ=1 AngleXU=0 Radius=2.7
    g3: Circle CenterX=84.95 CenterY=16.5 CenterZ=0 NormalX=0 NormalY=0 NormalZ=1 AngleXU=0 Radius=2.7
  constraints (4):
    c: Block(g3)
    c: Block(g2)
    c: Block(g0)
    c: Block(g1)
FEATURE [Part::Extrusion] Extrude019  label="removeSolenoidAdjusterHoles"
  Base = -> Sketch019
  Dir = (0,-1,1.1e-15)
  DirMode = 2
  FaceMakerClass = Part::FaceMakerBullseye
  LengthFwd = 6
  LengthRev = 0
  Placement = pos=(0,-30,0) rot=(0,0,1;0rad)
  Solid = true
  Symmetric = false
FEATURE [Sketcher::SketchObject] Sketch020
  FullyConstrained = true
  Placement = pos=(0,-14.3,2.37) rot=(-1,0,0;2.03453rad)
  sketch-geometry (6):
    g0: LineSegment StartX=45.5 StartY=-21.2 StartZ=0 EndX=49.5 EndY=-21.2 EndZ=0
    g1: LineSegment StartX=45.5 StartY=0 StartZ=0 EndX=49.5 EndY=0 EndZ=0
    g2: LineSegment StartX=49.5 StartY=0 StartZ=0 EndX=49.5 EndY=-21.2 EndZ=0
    g3: LineSegment StartX=4 StartY=0 StartZ=0 EndX=4 EndY=-21.2 EndZ=0
    g4: LineSegment StartX=45.5 StartY=-21.2 StartZ=0 EndX=4 EndY=-21.2 EndZ=0
    g5: LineSegment StartX=4 StartY=0 StartZ=0 EndX=45.5 EndY=0 EndZ=0
  constraints (16):
    c: Horizontal(g0)
    c: Distance(g0) = 4
    c: Horizontal(g1)
    c: Distance(g1) = 4
    c: Coincident(g2,g1)
    c: Coincident(g2,g0)
    c: Vertical(g2)
    c: Block(g2)
    c: Vertical(g3)
    c: Coincident(g4,g0)
    c: Horizontal(g4)
    c: Coincident(g4,g3)
    c: Coincident(g5,g1)
    c: Horizontal(g5)
    c: Block(g3)
    c: Block(g5)
FEATURE [Part::Box] Box  label="Cube"
  AttacherType = Attacher::AttachEngine3D
  Height = 10
  Length = 190
  Placement = pos=(-30,0,0) rot=(0,0,1;0rad)
  Width = 10
FEATURE [Part::Fillet] Fillet008
  Base = -> Box
  Edges = 1 edges r=7.5: [Edge11]
FEATURE [Part::Box] Box001  label="Cube001"
  AttacherType = Attacher::AttachEngine3D
  Height = 10
  Length = 190
  Placement = pos=(-35,0,0) rot=(0,0,1;0rad)
  Width = 10
FEATURE [Part::Cut] Cut  label="filletMain"
  Base = -> Box001
  Placement = pos=(0,-10,0) rot=(0,0,1;0rad)
  Tool = -> Fillet008
FEATURE [Part::Box] Box002  label="Cube002"
  AttacherType = Attacher::AttachEngine3D
  Height = 30
  Length = 190
  Placement = pos=(-20,0,0) rot=(0,0,1;0rad)
  Width = 10
FEATURE [Part::Box] Box003  label="Cube003"
  AttacherType = Attacher::AttachEngine3D
  Height = 10
  Length = 190
  Placement = pos=(-90,-50,-10) rot=(0,0,1;0rad)
  Width = 50
FEATURE [Sketcher::SketchObject] Sketch021
  FullyConstrained = true
  Placement = pos=(0,-14.3,2.37) rot=(-1,0,0;2.03453rad)
  sketch-geometry (6):
    g0: LineSegment StartX=41.65 StartY=-3.15 StartZ=0 EndX=38.95 EndY=-3.15 EndZ=0
    g1: LineSegment StartX=36.25 StartY=-3.15 StartZ=0 EndX=38.95 EndY=-3.15 EndZ=0
    g2: LineSegment StartX=41.65 StartY=-3.15 StartZ=0 EndX=41.65 EndY=-7.15 EndZ=0
    g3: LineSegment StartX=38.95 StartY=-7.15 StartZ=0 EndX=41.65 EndY=-7.15 EndZ=0
    g4: LineSegment StartX=38.95 StartY=-7.15 StartZ=0 EndX=36.25 EndY=-7.15 EndZ=0
    g5: LineSegment StartX=36.25 StartY=-3.15 StartZ=0 EndX=36.25 EndY=-7.15 EndZ=0
  constraints (16):
    c: Horizontal(g0)
    c: Distance(g0) = 2.7
    c: Horizontal(g1)
    c: Distance(g1) = 2.7
    c: Coincident(g1,g0)
    c: Block(g0)
    c: Coincident(g2,g0)
    c: Vertical(g2)
    c: Horizontal(g3)
    c: Coincident(g3,g2)
    c: Horizontal(g4)
    c: Coincident(g5,g1)
    c: Vertical(g5)
    c: Coincident(g5,g4)
    c: Block(g3)
    c: Block(g4)
FEATURE [Sketcher::SketchObject] Sketch022
  FullyConstrained = true
  Placement = pos=(0,-14.3,2.37) rot=(-1,0,0;2.03453rad)
  sketch-geometry (6):
    g0: LineSegment StartX=41.65 StartY=-3.15 StartZ=0 EndX=38.95 EndY=-3.15 EndZ=0
    g1: LineSegment StartX=36.25 StartY=-3.15 StartZ=0 EndX=38.95 EndY=-3.15 EndZ=0
    g2: LineSegment StartX=41.65 StartY=-3.15 StartZ=0 EndX=41.65 EndY=-7.15 EndZ=0
    g3: LineSegment StartX=38.95 StartY=-7.15 StartZ=0 EndX=41.65 EndY=-7.15 EndZ=0
    g4: LineSegment StartX=38.95 StartY=-7.15 StartZ=0 EndX=36.25 EndY=-7.15 EndZ=0
    g5: LineSegment StartX=36.25 StartY=-3.15 StartZ=0 EndX=36.25 EndY=-7.15 EndZ=0
  constraints (16):
    c: Horizontal(g0)
    c: Distance(g0) = 2.7
    c: Horizontal(g1)
    c: Distance(g1) = 2.7
    c: Coincident(g1,g0)
    c: Block(g0)
    c: Coincident(g2,g0)
    c: Vertical(g2)
    c: Horizontal(g3)
    c: Coincident(g3,g2)
    c: Horizontal(g4)
    c: Coincident(g5,g1)
    c: Vertical(g5)
    c: Coincident(g5,g4)
    c: Block(g3)
    c: Block(g4)
FEATURE [Sketcher::SketchObject] Sketch024
  FullyConstrained = true
  Placement = pos=(0,-14.3,2.37) rot=(-1,0,0;2.03453rad)
  sketch-geometry (4):
    g0: LineSegment StartX=49.5 StartY=-21.2 StartZ=0 EndX=49.5 EndY=-22.8 EndZ=0
    g1: LineSegment StartX=49.5 StartY=-22.8 StartZ=0 EndX=0.002238 EndY=-22.8 EndZ=0
    g2: LineSegment StartX=0.002238 StartY=-21.2 StartZ=0 EndX=0.002238 EndY=-22.8 EndZ=0
    g3: LineSegment StartX=49.5 StartY=-21.2 StartZ=0 EndX=0.002238 EndY=-21.2 EndZ=0
  constraints (10):
    c: Vertical(g0)
    c: Distance(g0) = 1.6
    c: Coincident(g1,g0)
    c: Horizontal(g1)
    c: Vertical(g2)
    c: Coincident(g2,g1)
    c: Coincident(g3,g0)
    c: Coincident(g3,g2)
    c: Horizontal(g3)
    c: Block(g3)
FEATURE [Sketcher::SketchObject] Sketch025
  FullyConstrained = true
  Placement = pos=(0,-14.3,2.37) rot=(-1,0,0;2.03453rad)
  sketch-geometry (4):
    g0: LineSegment StartX=0 StartY=1.5 StartZ=0 EndX=0 EndY=0 EndZ=0
    g1: LineSegment StartX=0 StartY=1.5 StartZ=0 EndX=5 EndY=1.5 EndZ=0
    g2: LineSegment StartX=5 StartY=1.5 StartZ=0 EndX=5 EndY=0 EndZ=0
    g3: LineSegment StartX=0 StartY=0 StartZ=0 EndX=5 EndY=0 EndZ=0
  constraints (13):
    c: Vertical(g0)
    c: Distance(g0) = 1.5
    c: Horizontal(g1)
    c: Distance(g1) = 5
    c: Coincident(g1,g0)
    c: Vertical(g2)
    c: Distance(g2) = 1.5
    c: Coincident(g2,g1)
    c: Block(g1)
    c: Block(g2)
    c: Block(g0)
    c: Coincident(g3,g0)
    c: Coincident(g3,g2)
FEATURE [Part::Extrusion] Extrude022  label="solenoidDriverBottomLipTopExtrude014"
  Base = -> Sketch025
  Dir = (0,0.894389,-0.447291)
  DirMode = 2
  FaceMakerClass = Part::FaceMakerBullseye
  LengthFwd = -6.5
  LengthRev = 0
  Placement = pos=(0,-15.45,20.3) rot=(1,0,0;1.5708rad)
  Solid = true
  Symmetric = false
FEATURE [Part::Fillet] Fillet013  label="solenoidDriverBottomLipTopFillet006"
  Base = -> Extrude022
  Edges = 1 edges r=1.4: [Edge6]
  Placement = pos=(5,0,0) rot=(0,0,1;0rad)
FEATURE [Sketcher::SketchObject] Sketch026
  FullyConstrained = true
  Placement = pos=(0,-14.3,2.37) rot=(-1,0,0;2.03453rad)
  sketch-geometry (4):
    g0: LineSegment StartX=0 StartY=1.5 StartZ=0 EndX=0 EndY=0 EndZ=0
    g1: LineSegment StartX=0 StartY=1.5 StartZ=0 EndX=5 EndY=1.5 EndZ=0
    g2: LineSegment StartX=5 StartY=1.5 StartZ=0 EndX=5 EndY=0 EndZ=0
    g3: LineSegment StartX=0 StartY=0 StartZ=0 EndX=5 EndY=0 EndZ=0
  constraints (13):
    c: Vertical(g0)
    c: Distance(g0) = 1.5
    c: Horizontal(g1)
    c: Distance(g1) = 5
    c: Coincident(g1,g0)
    c: Vertical(g2)
    c: Distance(g2) = 1.5
    c: Coincident(g2,g1)
    c: Block(g1)
    c: Block(g2)
    c: Block(g0)
    c: Coincident(g3,g0)
    c: Coincident(g3,g2)
FEATURE [Part::Extrusion] Extrude023  label="solenoidDriverBottomLipTopExtrude015"
  Base = -> Sketch026
  Dir = (0,0.894389,-0.447291)
  DirMode = 2
  FaceMakerClass = Part::FaceMakerBullseye
  LengthFwd = -6.5
  LengthRev = 0
  Placement = pos=(5,-14.15,19.65) rot=(1,0,0;1.5708rad)
  Solid = true
  Symmetric = false
FEATURE [Sketcher::SketchObject] Sketch027
  FullyConstrained = true
  Placement = pos=(0,-14.3,2.37) rot=(-1,0,0;2.03453rad)
  sketch-geometry (5):
    g0: LineSegment StartX=45.5 StartY=-21.2 StartZ=0 EndX=49.5 EndY=-21.2 EndZ=0
    g1: LineSegment StartX=49.5 StartY=0 StartZ=0 EndX=49.5 EndY=-21.2 EndZ=0
    g2: LineSegment StartX=49.5 StartY=0 StartZ=0 EndX=49.5 EndY=1.6 EndZ=0
    g3: LineSegment StartX=45.5 StartY=-21.2 StartZ=0 EndX=45.5 EndY=1.6 EndZ=0
    g4: LineSegment StartX=49.5 StartY=1.6 StartZ=0 EndX=45.5 EndY=1.6 EndZ=0
  constraints (14):
    c: Horizontal(g0)
    c: Distance(g0) = 4
    c: Coincident(g1,g0)
    c: Vertical(g1)
    c: Block(g1)
    c: Vertical(g2)
    c: Distance(g2) = 1.6
    c: Block(g2)
    c: Coincident(g3,g0)
    c: Vertical(g3)
    c: Coincident(g4,g2)
    c: Horizontal(g4)
    c: Block(g0)
    c: Coincident(g3,g4)
FEATURE [Part::Extrusion] Extrude024
  Base = -> Sketch027
  Dir = (0,0.894389,-0.447291)
  DirMode = 2
  FaceMakerClass = Part::FaceMakerBullseye
  LengthFwd = 6.34
  LengthRev = 0
  Placement = pos=(0,-5.59,1) rot=(0,0,1;0rad)
  Solid = true
  Symmetric = false
FEATURE [Part::Fillet] Fillet014  label="solenoidDriverSideBarFillet014"
  Base = -> Extrude024
  Edges = 1 edges r=1.4: [Edge14]
  Placement = pos=(0,0.9,-0.45) rot=(0,0,1;0rad)
FEATURE [Part::Revolution] Revolve  label="mainScrewStandRevolve"
  Angle = 360
  Axis = (0,0,1)
  Base = (0,0,0)
  FaceMakerClass = Part::FaceMakerBullseye
  Placement = pos=(121.35,-15.3,0) rot=(0,0,1;0rad)
  Solid = true
  Source = -> Sketch004
  Symmetric = false
FEATURE [Part::Extrusion] Extrude021  label="solenoidDriverTopLipLowerExtrude011"
  Base = -> Sketch024
  Dir = (0,0.894389,-0.447291)
  DirMode = 2
  FaceMakerClass = Part::FaceMakerBullseye
  LengthFwd = 5.05
  LengthRev = 0
  Solid = true
  Symmetric = false
FEATURE [Part::Fillet] Fillet012  label="solenoidDriverTopLipLowerFillet004"
  Base = -> Extrude021
  Edges = 1 edges r=1.2: [Edge7]
  Placement = pos=(0,-0.9,-1.35) rot=(0,0,1;0rad)
FEATURE [Part::Fillet] Fillet003  label="solenoidDriverTopLipLowerFillet003"
  Base = -> Extrude010
  Edges = 1 edges r=1.2: [Edge7]
  Placement = pos=(0,-3,-0.3) rot=(0,0,1;0rad)
FEATURE [Part::Extrusion] Extrude025  label="mainBodyUpperExtrude025"
  Base = -> Sketch001
  Dir = (0,0,1)
  DirMode = 2
  FaceMakerClass = Part::FaceMakerBullseye
  LengthFwd = 20
  LengthRev = 0
  Solid = true
  Symmetric = false
FEATURE [Part::MultiFuse] Fusion  label="solenoidDriverBottomLipFusion"
  Placement = pos=(0,-1.6,0) rot=(0,0,1;0rad)
  Shapes = -> [Fillet005,Fillet013,Extrude023,Extrude013]
FEATURE [Sketcher::SketchObject] Sketch028
  FullyConstrained = true
  Placement = pos=(0,-14.3,2.37) rot=(-1,0,0;2.03453rad)
  sketch-geometry (4):
    g0: LineSegment StartX=0 StartY=1.5 StartZ=0 EndX=0 EndY=0 EndZ=0
    g1: LineSegment StartX=0 StartY=1.5 StartZ=0 EndX=5 EndY=1.5 EndZ=0
    g2: LineSegment StartX=5 StartY=1.5 StartZ=0 EndX=5 EndY=0 EndZ=0
    g3: LineSegment StartX=0 StartY=0 StartZ=0 EndX=5 EndY=0 EndZ=0
  constraints (13):
    c: Vertical(g0)
    c: Distance(g0) = 1.5
    c: Horizontal(g1)
    c: Distance(g1) = 5
    c: Coincident(g1,g0)
    c: Vertical(g2)
    c: Distance(g2) = 1.5
    c: Coincident(g2,g1)
    c: Block(g1)
    c: Block(g2)
    c: Block(g0)
    c: Coincident(g3,g0)
    c: Coincident(g3,g2)
FEATURE [Part::Extrusion] Extrude026  label="solenoidDriverBottomLipTopExtrude016"
  Base = -> Sketch028
  Dir = (0,0.894389,-0.447291)
  DirMode = 2
  FaceMakerClass = Part::FaceMakerBullseye
  LengthFwd = -6.5
  LengthRev = 0
  Placement = pos=(5,-14.15,19.65) rot=(1,0,0;1.5708rad)
  Solid = true
  Symmetric = false
FEATURE [Sketcher::SketchObject] Sketch029
  FullyConstrained = true
  Placement = pos=(0,-14.3,2.37) rot=(-1,0,0;2.03453rad)
  sketch-geometry (4):
    g0: LineSegment StartX=0 StartY=1.5 StartZ=0 EndX=0 EndY=0 EndZ=0
    g1: LineSegment StartX=0 StartY=1.5 StartZ=0 EndX=5 EndY=1.5 EndZ=0
    g2: LineSegment StartX=5 StartY=1.5 StartZ=0 EndX=5 EndY=0 EndZ=0
    g3: LineSegment StartX=0 StartY=0 StartZ=0 EndX=5 EndY=0 EndZ=0
  constraints (13):
    c: Vertical(g0)
    c: Distance(g0) = 1.5
    c: Horizontal(g1)
    c: Distance(g1) = 5
    c: Coincident(g1,g0)
    c: Vertical(g2)
    c: Distance(g2) = 1.5
    c: Coincident(g2,g1)
    c: Block(g1)
    c: Block(g2)
    c: Block(g0)
    c: Coincident(g3,g0)
    c: Coincident(g3,g2)
FEATURE [Part::Extrusion] Extrude027  label="solenoidDriverBottomLipTopExtrude017"
  Base = -> Sketch029
  Dir = (0,0.894389,-0.447291)
  DirMode = 2
  FaceMakerClass = Part::FaceMakerBullseye
  LengthFwd = -6.5
  LengthRev = 0
  Placement = pos=(0,-14.15,19.65) rot=(1,0,0;1.5708rad)
  Solid = true
  Symmetric = false
FEATURE [Sketcher::SketchObject] Sketch030
  FullyConstrained = true
  Placement = pos=(0,-14.3,2.37) rot=(-1,0,0;2.03453rad)
  sketch-geometry (4):
    g0: LineSegment StartX=0 StartY=1.5 StartZ=0 EndX=0 EndY=0 EndZ=0
    g1: LineSegment StartX=0 StartY=1.5 StartZ=0 EndX=5 EndY=1.5 EndZ=0
    g2: LineSegment StartX=5 StartY=1.5 StartZ=0 EndX=5 EndY=0 EndZ=0
    g3: LineSegment StartX=0 StartY=0 StartZ=0 EndX=5 EndY=0 EndZ=0
  constraints (13):
    c: Vertical(g0)
    c: Distance(g0) = 1.5
    c: Horizontal(g1)
    c: Distance(g1) = 5
    c: Coincident(g1,g0)
    c: Vertical(g2)
    c: Distance(g2) = 1.5
    c: Coincident(g2,g1)
    c: Block(g1)
    c: Block(g2)
    c: Block(g0)
    c: Coincident(g3,g0)
    c: Coincident(g3,g2)
FEATURE [Sketcher::SketchObject] Sketch031
  FullyConstrained = true
  Placement = pos=(0,-14.3,2.37) rot=(-1,0,0;2.03453rad)
  sketch-geometry (6):
    g0: LineSegment StartX=45.5 StartY=-21.2 StartZ=0 EndX=49.5 EndY=-21.2 EndZ=0
    g1: LineSegment StartX=45.5 StartY=0 StartZ=0 EndX=49.5 EndY=0 EndZ=0
    g2: LineSegment StartX=49.5 StartY=0 StartZ=0 EndX=49.5 EndY=-21.2 EndZ=0
    g3: LineSegment StartX=4 StartY=0 StartZ=0 EndX=4 EndY=-21.2 EndZ=0
    g4: LineSegment StartX=45.5 StartY=-21.2 StartZ=0 EndX=4 EndY=-21.2 EndZ=0
    g5: LineSegment StartX=4 StartY=0 StartZ=0 EndX=45.5 EndY=0 EndZ=0
  constraints (16):
    c: Horizontal(g0)
    c: Distance(g0) = 4
    c: Horizontal(g1)
    c: Distance(g1) = 4
    c: Coincident(g2,g1)
    c: Coincident(g2,g0)
    c: Vertical(g2)
    c: Block(g2)
    c: Vertical(g3)
    c: Coincident(g4,g0)
    c: Horizontal(g4)
    c: Coincident(g4,g3)
    c: Coincident(g5,g1)
    c: Horizontal(g5)
    c: Block(g3)
    c: Block(g5)
FEATURE [Part::Extrusion] Extrude028  label="removeFromSolenoidDriverMainExtrude021"
  Base = -> Sketch031
  Dir = (0,0.894389,-0.447291)
  DirMode = 2
  FaceMakerClass = Part::FaceMakerBullseye
  LengthFwd = 3.1
  LengthRev = 0
  Placement = pos=(-4,-2.42,-0.8) rot=(0,0,1;0rad)
  Solid = true
  Symmetric = false
FEATURE [Part::Extrusion] Extrude029  label="solenoidDriverBottomLipTopExtrude018"
  Base = -> Sketch030
  Dir = (0,0.894389,-0.447291)
  DirMode = 2
  FaceMakerClass = Part::FaceMakerBullseye
  LengthFwd = -6.5
  LengthRev = 0
  Placement = pos=(5,-14.15,19.65) rot=(1,0,0;1.5708rad)
  Solid = true
  Symmetric = false
FEATURE [Sketcher::SketchObject] Sketch032
  FullyConstrained = true
  Placement = pos=(0,-14.3,2.37) rot=(-1,0,0;2.03453rad)
  sketch-geometry (4):
    g0: LineSegment StartX=0 StartY=1.5 StartZ=0 EndX=0 EndY=0 EndZ=0
    g1: LineSegment StartX=0 StartY=1.5 StartZ=0 EndX=5 EndY=1.5 EndZ=0
    g2: LineSegment StartX=5 StartY=1.5 StartZ=0 EndX=5 EndY=0 EndZ=0
    g3: LineSegment StartX=0 StartY=0 StartZ=0 EndX=5 EndY=0 EndZ=0
  constraints (13):
    c: Vertical(g0)
    c: Distance(g0) = 1.5
    c: Horizontal(g1)
    c: Distance(g1) = 5
    c: Coincident(g1,g0)
    c: Vertical(g2)
    c: Distance(g2) = 1.5
    c: Coincident(g2,g1)
    c: Block(g1)
    c: Block(g2)
    c: Block(g0)
    c: Coincident(g3,g0)
    c: Coincident(g3,g2)
FEATURE [Part::Extrusion] Extrude030  label="solenoidDriverBottomLipTopExtrude019"
  Base = -> Sketch032
  Dir = (0,0.894389,-0.447291)
  DirMode = 2
  FaceMakerClass = Part::FaceMakerBullseye
  LengthFwd = -6.5
  LengthRev = 0
  Placement = pos=(0,-14.15,19.65) rot=(1,0,0;1.5708rad)
  Solid = true
  Symmetric = false
FEATURE [Part::MultiFuse] Fusion004
  Placement = pos=(0,1.4,2.65) rot=(0,0,1;0rad)
  Shapes = -> [Extrude029,Extrude030]
FEATURE [Part::MultiFuse] Fusion003
  Placement = pos=(-2.3,0,0) rot=(0,0,1;0rad)
  Shapes = -> [Extrude028,Fusion004]
FEATURE [Sketcher::SketchObject] Sketch033
  FullyConstrained = true
  Placement = pos=(0,-14.3,2.37) rot=(-1,0,0;2.03453rad)
  sketch-geometry (4):
    g0: LineSegment StartX=0 StartY=1.5 StartZ=0 EndX=0 EndY=0 EndZ=0
    g1: LineSegment StartX=0 StartY=1.5 StartZ=0 EndX=5 EndY=1.5 EndZ=0
    g2: LineSegment StartX=5 StartY=1.5 StartZ=0 EndX=5 EndY=0 EndZ=0
    g3: LineSegment StartX=0 StartY=0 StartZ=0 EndX=5 EndY=0 EndZ=0
  constraints (13):
    c: Vertical(g0)
    c: Distance(g0) = 1.5
    c: Horizontal(g1)
    c: Distance(g1) = 5
    c: Coincident(g1,g0)
    c: Vertical(g2)
    c: Distance(g2) = 1.5
    c: Coincident(g2,g1)
    c: Block(g1)
    c: Block(g2)
    c: Block(g0)
    c: Coincident(g3,g0)
    c: Coincident(g3,g2)
FEATURE [Sketcher::SketchObject] Sketch034
  FullyConstrained = true
  Placement = pos=(0,-14.3,2.37) rot=(-1,0,0;2.03453rad)
  sketch-geometry (4):
    g0: LineSegment StartX=0 StartY=1.5 StartZ=0 EndX=0 EndY=0 EndZ=0
    g1: LineSegment StartX=0 StartY=1.5 StartZ=0 EndX=5 EndY=1.5 EndZ=0
    g2: LineSegment StartX=5 StartY=1.5 StartZ=0 EndX=5 EndY=0 EndZ=0
    g3: LineSegment StartX=0 StartY=0 StartZ=0 EndX=5 EndY=0 EndZ=0
  constraints (13):
    c: Vertical(g0)
    c: Distance(g0) = 1.5
    c: Horizontal(g1)
    c: Distance(g1) = 5
    c: Coincident(g1,g0)
    c: Vertical(g2)
    c: Distance(g2) = 1.5
    c: Coincident(g2,g1)
    c: Block(g1)
    c: Block(g2)
    c: Block(g0)
    c: Coincident(g3,g0)
    c: Coincident(g3,g2)
FEATURE [Part::Extrusion] Extrude020  label="removeFromSolenoidDriverMainExtrude020"
  Base = -> Sketch020
  Dir = (0,0.894389,-0.447291)
  DirMode = 2
  FaceMakerClass = Part::FaceMakerBullseye
  LengthFwd = 3.1
  LengthRev = 0
  Placement = pos=(-4,-2.42,-0.8) rot=(0,0,1;0rad)
  Solid = true
  Symmetric = false
FEATURE [Part::Fillet] Fillet
  Base = -> Fusion003
  Edges = 1 edges r=10: [Edge5]
  Placement = pos=(-2,0,0) rot=(0,0,1;0rad)
FEATURE [Part::MultiFuse] Fusion001
  Placement = pos=(0,1.4,2.65) rot=(0,0,1;0rad)
  Shapes = -> [Extrude026,Extrude027]
FEATURE [Part::MultiFuse] Fusion002
  Shapes = -> [Extrude020,Fusion001]
FEATURE [Sketcher::SketchObject] Sketch035
  FullyConstrained = true
  Placement = pos=(0,-14.3,2.37) rot=(-1,0,0;2.03453rad)
  sketch-geometry (4):
    g0: LineSegment StartX=0 StartY=1.5 StartZ=0 EndX=0 EndY=0 EndZ=0
    g1: LineSegment StartX=0 StartY=1.5 StartZ=0 EndX=5 EndY=1.5 EndZ=0
    g2: LineSegment StartX=5 StartY=1.5 StartZ=0 EndX=5 EndY=0 EndZ=0
    g3: LineSegment StartX=0 StartY=0 StartZ=0 EndX=5 EndY=0 EndZ=0
  constraints (13):
    c: Vertical(g0)
    c: Distance(g0) = 1.5
    c: Horizontal(g1)
    c: Distance(g1) = 5
    c: Coincident(g1,g0)
    c: Vertical(g2)
    c: Distance(g2) = 1.5
    c: Coincident(g2,g1)
    c: Block(g1)
    c: Block(g2)
    c: Block(g0)
    c: Coincident(g3,g0)
    c: Coincident(g3,g2)
FEATURE [Sketcher::SketchObject] Sketch036
  FullyConstrained = true
  Placement = pos=(0,-14.3,2.37) rot=(-1,0,0;2.03453rad)
  sketch-geometry (4):
    g0: LineSegment StartX=0 StartY=1.5 StartZ=0 EndX=0 EndY=0 EndZ=0
    g1: LineSegment StartX=0 StartY=1.5 StartZ=0 EndX=5 EndY=1.5 EndZ=0
    g2: LineSegment StartX=5 StartY=1.5 StartZ=0 EndX=5 EndY=0 EndZ=0
    g3: LineSegment StartX=0 StartY=0 StartZ=0 EndX=5 EndY=0 EndZ=0
  constraints (13):
    c: Vertical(g0)
    c: Distance(g0) = 1.5
    c: Horizontal(g1)
    c: Distance(g1) = 5
    c: Coincident(g1,g0)
    c: Vertical(g2)
    c: Distance(g2) = 1.5
    c: Coincident(g2,g1)
    c: Block(g1)
    c: Block(g2)
    c: Block(g0)
    c: Coincident(g3,g0)
    c: Coincident(g3,g2)
FEATURE [Part::Extrusion] Extrude031  label="solenoidDriverBottomLipTopExtrude020"
  Base = -> Sketch035
  Dir = (0,0.894389,-0.447291)
  DirMode = 2
  FaceMakerClass = Part::FaceMakerBullseye
  LengthFwd = -6.5
  LengthRev = 0
  Placement = pos=(5,-14.15,19.65) rot=(1,0,0;1.5708rad)
  Solid = true
  Symmetric = false
FEATURE [Part::Extrusion] Extrude032  label="solenoidDriverBottomLipTopExtrude021"
  Base = -> Sketch036
  Dir = (0,0.894389,-0.447291)
  DirMode = 2
  FaceMakerClass = Part::FaceMakerBullseye
  LengthFwd = -6.5
  LengthRev = 0
  Placement = pos=(0,-14.15,19.65) rot=(1,0,0;1.5708rad)
  Solid = true
  Symmetric = false
FEATURE [Part::MultiFuse] Fusion009
  Placement = pos=(8,1.4,2.65) rot=(0,0,1;0rad)
  Shapes = -> [Extrude031,Extrude032]
FEATURE [Part::MultiFuse] Fusion010  label="removeFromSolenoidDriver"
  Shapes = -> [Fusion009,Fillet,Fusion002]
FEATURE [Sketcher::SketchObject] Sketch037
  FullyConstrained = true
  Placement = pos=(0,0,0) rot=(1,0,0;1.5708rad)
  sketch-geometry (4):
    g0: Circle CenterX=64.05 CenterY=16.5 CenterZ=0 NormalX=0 NormalY=0 NormalZ=1 AngleXU=0 Radius=2.7
    g1: Circle CenterX=64.05 CenterY=8.5 CenterZ=0 NormalX=0 NormalY=0 NormalZ=1 AngleXU=0 Radius=2.7
    g2: Circle CenterX=84.15 CenterY=8.5 CenterZ=0 NormalX=0 NormalY=0 NormalZ=1 AngleXU=0 Radius=2.7
    g3: Circle CenterX=84.15 CenterY=16.5 CenterZ=0 NormalX=0 NormalY=0 NormalZ=1 AngleXU=0 Radius=2.7
  constraints (4):
    c: Block(g2)
    c: Block(g3)
    c: Block(g0)
    c: Block(g1)
FEATURE [Part::Extrusion] Extrude033  label="removeFromMainBodyToCreateScrewHoleCounterSinks001"
  Base = -> Sketch037
  Dir = (0,-1,1.1e-15)
  DirMode = 2
  FaceMakerClass = Part::FaceMakerBullseye
  LengthFwd = 1.9
  LengthRev = 0
  Placement = pos=(0.8,0,0) rot=(0,0,1;0rad)
  Solid = true
  Symmetric = false
FEATURE [Part::MultiFuse] Fusion011  label="removeFromMainBodyToCreateScrewHoleCounterSinks001Fusion011"
  Shapes = -> [Extrude014,Extrude033]
FEATURE [Sketcher::SketchObject] Sketch038
  FullyConstrained = true
  Placement = pos=(0,-14.3,2.37) rot=(-1,0,0;2.03453rad)
  sketch-geometry (4):
    g0: LineSegment StartX=33.9 StartY=-9.7 StartZ=0 EndX=33.9 EndY=-1.5 EndZ=0
    g1: LineSegment StartX=33.9 StartY=-1.5 StartZ=0 EndX=44.5 EndY=-1.5 EndZ=0
    g2: LineSegment StartX=33.9 StartY=-9.7 StartZ=0 EndX=44.5 EndY=-9.7 EndZ=0
    g3: LineSegment StartX=44.5 StartY=-1.5 StartZ=0 EndX=44.5 EndY=-9.7 EndZ=0
  constraints (10):
    c: Vertical(g0)
    c: Coincident(g1,g0)
    c: Horizontal(g1)
    c: Block(g1)
    c: Block(g0)
    c: Coincident(g2,g0)
    c: Horizontal(g2)
    c: Coincident(g3,g1)
    c: Coincident(g3,g2)
    c: Vertical(g3)
FEATURE [Part::Extrusion] Extrude034
  Base = -> Sketch038
  Dir = (0,0.894389,-0.447291)
  DirMode = 2
  FaceMakerClass = Part::FaceMakerBullseye
  LengthFwd = 16
  LengthRev = 0
  Placement = pos=(0,-22,7) rot=(0,0,1;0rad)
  Solid = true
  Symmetric = false
FEATURE [Sketcher::SketchObject] Sketch039
  FullyConstrained = true
  Placement = pos=(0,-14.3,2.37) rot=(-1,0,0;2.03453rad)
  sketch-geometry (4):
    g0: LineSegment StartX=5.5 StartY=-7.7 StartZ=0 EndX=13.3 EndY=-7.7 EndZ=0
    g1: LineSegment StartX=13.3 StartY=-7.7 StartZ=0 EndX=13.3 EndY=-13.1 EndZ=0
    g2: LineSegment StartX=13.3 StartY=-13.1 StartZ=0 EndX=5.5 EndY=-13.1 EndZ=0
    g3: LineSegment StartX=5.5 StartY=-7.7 StartZ=0 EndX=5.5 EndY=-13.1 EndZ=0
  constraints (12):
    c: Horizontal(g0)
    c: Distance(g0) = 7.8
    c: Coincident(g1,g0)
    c: Vertical(g1)
    c: Distance(g1) = 5.4
    c: Coincident(g2,g1)
    c: Horizontal(g2)
    c: Vertical(g3)
    c: Coincident(g3,g2)
    c: Block(g0)
    c: Block(g2)
    c: Block(g3)
FEATURE [Part::Extrusion] Extrude035  label="removeToMakeHoleForConnectorExtrude035"
  Base = -> Sketch039
  Dir = (0,0.894389,-0.447291)
  DirMode = 2
  FaceMakerClass = Part::FaceMakerBullseye
  LengthFwd = 15
  LengthRev = 0
  Placement = pos=(-4,-22,9.6469) rot=(0,0,1;0rad)
  Solid = true
  Symmetric = false
FEATURE [App::MeasureDistance] Distance  label="Distance: 4.00 mm"
  Distance = 4.00184
  P1 = (119.349,-15.3,8)
  P2 = (123.351,-15.3,8)
FEATURE [App::MeasureDistance] Distance001  label="Distance: 3.80 mm"
  Distance = 3.8
  P1 = (119.45,-15.3,8)
  P2 = (123.25,-15.3,8)
FEATURE [Part::Fillet] Fillet015
  Base = -> Extrude009
  Edges = 1 edges r=1.59: [Edge7]
FEATURE [Part::Fillet] Fillet016
  Base = -> Extrude017
  Edges = 1 edges r=1.49: [Edge12]
FEATURE [Part::Fillet] Fillet017
  Base = -> Fillet016
  Edges = 1 edges r=1.45: [Edge8]
FEATURE [Part::MultiFuse] Fusion012  label="main"
  Shapes = -> [Extrude,Revolve,Extrude005,Fillet003,Fillet012,Fillet014,Extrude025,Fusion,Fillet015,Fillet017]
FEATURE [Part::Cut] Cut001
  Base = -> Fusion012
  Tool = -> Box003
FEATURE [Part::Cut] Cut002
  Base = -> Cut001
  Tool = -> Box002
FEATURE [Part::Cut] Cut003
  Base = -> Cut002
  Tool = -> Cut
FEATURE [Part::Cut] Cut004
  Base = -> Cut003
  Tool = -> Extrude019
FEATURE [Part::Cut] Cut005
  Base = -> Cut004
  Tool = -> Fusion011
FEATURE [Part::Cut] Cut006
  Base = -> Cut005
  Tool = -> Extrude004
FEATURE [Part::Cut] Cut007
  Base = -> Cut006
  Tool = -> Extrude015
FEATURE [Part::Cut] Cut008
  Base = -> Cut007
  Tool = -> Extrude008
FEATURE [Part::Cut] Cut009
  Base = -> Cut008
  Tool = -> Fusion010
FEATURE [App::MeasureDistance] Distance002  label="Distance: 2.05 mm"
  Distance = 2.05453
  P1 = (1.5,-23.0732,21.402)
  P2 = (6e-15,-23,20)
FEATURE [Part::Cut] Cut010
  Base = -> Cut009
  Tool = -> Extrude035
FEATURE [Part::Cut] Cut011
  Base = -> Cut010
  Tool = -> Extrude034
FEATURE [Part::Fillet] Fillet018
  Base = -> Cut011
  Edges = 1 edges r=3: [Edge134]
FEATURE [Part::Fillet] Fillet019
  Base = -> Fillet018
  Edges = 1 edges r=3: [Edge29]
FEATURE [Part::Box] Box004  label="Cube004"
  AttacherType = Attacher::AttachEngine3D
  Height = 10
  Length = 200
  Placement = pos=(-30,0,0) rot=(0,0,1;0rad)
  Width = 10
FEATURE [Part::Fillet] Fillet020
  Base = -> Box004
  Edges = 1 edges r=3.6: [Edge12]
FEATURE [Part::Box] Box005  label="Cube005"
  AttacherType = Attacher::AttachEngine3D
  Height = 10
  Length = 198
  Placement = pos=(-30,0,0) rot=(0,0,1;0rad)
  Width = 10
FEATURE [Part::Cut] Cut012
  Base = -> Box005
  Tool = -> Fillet020
FEATURE [Part::Box] Box006  label="Cube006"
  AttacherType = Attacher::AttachEngine3D
  Height = 5
  Length = 200
  Placement = pos=(-30,6.4,10) rot=(1,0,0;0rad)
  Width = 5
FEATURE [Part::Box] Box007  label="Cube007"
  AttacherType = Attacher::AttachEngine3D
  Height = 5
  Length = 200
  Placement = pos=(-30,6.4,10) rot=(1,0,0;0.872665rad)
  Width = 5
FEATURE [Part::MultiFuse] Fusion013  label="removeFromMainFusion013"
  Placement = pos=(0,-10,10) rot=(0,0,1;0rad)
  Shapes = -> [Box007,Box006,Cut012]
FEATURE [Part::Cut] Cut013
  Base = -> Fillet019
  Tool = -> Fusion013
FEATURE [Mesh::Feature] v0_98_Cut013  label="v0_98-Cut013"
FEATURE [App::MeasureDistance] Distance003  label="Distance: 7.18 mm"
  Distance = 7.17719
  P1 = (117.773,-15.3145,-2.4)
  P2 = (124.951,-15.2973,-2.4)
FEATURE [Sketcher::SketchObject] Sketch040
  FullyConstrained = true
  Placement = pos=(0,-14.3,2.37) rot=(-1,0,0;2.03453rad)
  sketch-geometry (4):
    g0: LineSegment StartX=0 StartY=1.5 StartZ=0 EndX=0 EndY=0 EndZ=0
    g1: LineSegment StartX=0 StartY=1.5 StartZ=0 EndX=5 EndY=1.5 EndZ=0
    g2: LineSegment StartX=5 StartY=1.5 StartZ=0 EndX=5 EndY=0 EndZ=0
    g3: LineSegment StartX=0 StartY=0 StartZ=0 EndX=5 EndY=0 EndZ=0
  constraints (13):
    c: Vertical(g0)
    c: Distance(g0) = 1.5
    c: Horizontal(g1)
    c: Distance(g1) = 5
    c: Coincident(g1,g0)
    c: Vertical(g2)
    c: Distance(g2) = 1.5
    c: Coincident(g2,g1)
    c: Block(g1)
    c: Block(g2)
    c: Block(g0)
    c: Coincident(g3,g0)
    c: Coincident(g3,g2)
FEATURE [Part::Extrusion] Extrude036
  Base = -> Sketch040
  Dir = (0,0.894389,-0.447291)
  DirMode = 2
  FaceMakerClass = Part::FaceMakerBullseye
  LengthFwd = 1.4
  LengthRev = 0
  Placement = pos=(0,8.25,17.58) rot=(0,0,1;0rad)
  Solid = true
  Symmetric = false
FEATURE [Sketcher::SketchObject] Sketch041
  FullyConstrained = true
  Placement = pos=(0,-14.3,2.37) rot=(-1,0,0;2.03453rad)
  sketch-geometry (4):
    g0: LineSegment StartX=0 StartY=1.5 StartZ=0 EndX=0 EndY=0 EndZ=0
    g1: LineSegment StartX=0 StartY=1.5 StartZ=0 EndX=5 EndY=1.5 EndZ=0
    g2: LineSegment StartX=5 StartY=1.5 StartZ=0 EndX=5 EndY=0 EndZ=0
    g3: LineSegment StartX=0 StartY=0 StartZ=0 EndX=5 EndY=0 EndZ=0
  constraints (13):
    c: Vertical(g0)
    c: Distance(g0) = 1.5
    c: Horizontal(g1)
    c: Distance(g1) = 5
    c: Coincident(g1,g0)
    c: Vertical(g2)
    c: Distance(g2) = 1.5
    c: Coincident(g2,g1)
    c: Block(g1)
    c: Block(g2)
    c: Block(g0)
    c: Coincident(g3,g0)
    c: Coincident(g3,g2)
FEATURE [Part::Extrusion] Extrude037
  Base = -> Sketch041
  Dir = (0,0.894389,-0.447291)
  DirMode = 2
  FaceMakerClass = Part::FaceMakerBullseye
  LengthFwd = 1.4
  LengthRev = 0
  Placement = pos=(0,6.11,13.33) rot=(0,0,1;0rad)
  Solid = true
  Symmetric = false
FEATURE [Part::MultiFuse] Fusion014  label="screwSpacerFusion014"
  Shapes = -> [Extrude037,Extrude036]
FEATURE [Sketcher::SketchObject] Sketch042
  FullyConstrained = true
  Placement = pos=(0,-14.3,2.37) rot=(-1,0,0;2.03453rad)
  sketch-geometry (4):
    g0: LineSegment StartX=0 StartY=1.5 StartZ=0 EndX=0 EndY=0 EndZ=0
    g1: LineSegment StartX=0 StartY=1.5 StartZ=0 EndX=5 EndY=1.5 EndZ=0
    g2: LineSegment StartX=5 StartY=1.5 StartZ=0 EndX=5 EndY=0 EndZ=0
    g3: LineSegment StartX=0 StartY=0 StartZ=0 EndX=5 EndY=0 EndZ=0
  constraints (13):
    c: Vertical(g0)
    c: Distance(g0) = 1.5
    c: Horizontal(g1)
    c: Distance(g1) = 5
    c: Coincident(g1,g0)
    c: Vertical(g2)
    c: Distance(g2) = 1.5
    c: Coincident(g2,g1)
    c: Block(g1)
    c: Block(g2)
    c: Block(g0)
    c: Coincident(g3,g0)
    c: Coincident(g3,g2)
FEATURE [Part::Extrusion] Extrude038
  Base = -> Sketch042
  Dir = (0,0.894389,-0.447291)
  DirMode = 2
  FaceMakerClass = Part::FaceMakerBullseye
  LengthFwd = 1.4
  LengthRev = 0
  Placement = pos=(0,8.459,18) rot=(0,0,1;0rad)
  Solid = true
  Symmetric = false
FEATURE [Part::MultiFuse] Fusion015  label="screwSpacerFusion014Fusion015"
  Placement = pos=(0,0.35,-0.18) rot=(0,0,1;0rad)
  Shapes = -> [Extrude038,Fusion014]
FEATURE [Part::Cylinder] Cylinder
  Angle = 360
  AttacherType = Attacher::AttachEngine3D
  Height = 10
  Placement = pos=(0,10,0) rot=(0,0,1;0rad)
  Radius = 1.5
FEATURE [Part::Cylinder] Cylinder001
  Angle = 360
  AttacherType = Attacher::AttachEngine3D
  Height = 10
  Placement = pos=(3,10,0) rot=(0,0,1;0rad)
  Radius = 1.5
FEATURE [Part::Box] Box008  label="Cube008"
  AttacherType = Attacher::AttachEngine3D
  Height = 10
  Length = 3
  Placement = pos=(0,8.5,0) rot=(0,0,1;0rad)
  Width = 3
FEATURE [Part::MultiFuse] Fusion016  label="holeForWireFusion016"
  Shapes = -> [Cylinder001,Box008,Cylinder]
FEATURE [Part::Box] Box009  label="Cube009"
  AttacherType = Attacher::AttachEngine3D
  Height = 10
  Length = 3
  Placement = pos=(0,8.5,0) rot=(0,0,1;0rad)
  Width = 3
FEATURE [Part::Cylinder] Cylinder002
  Angle = 360
  AttacherType = Attacher::AttachEngine3D
  Height = 10
  Placement = pos=(0,10,0) rot=(0,0,1;0rad)
  Radius = 1.5
FEATURE [Part::Cylinder] Cylinder003
  Angle = 360
  AttacherType = Attacher::AttachEngine3D
  Height = 10
  Placement = pos=(3,10,0) rot=(0,0,1;0rad)
  Radius = 1.5
FEATURE [Part::MultiFuse] Fusion017  label="holeForWireFusion017"
  Placement = pos=(0,0,10) rot=(0,0,1;0rad)
  Shapes = -> [Cylinder003,Box009,Cylinder002]
FEATURE [Part::MultiFuse] Fusion018  label="holeForWireFusion018"
  Placement = pos=(0,0,0) rot=(0,1,0;-1.5708rad)
  Shapes = -> [Fusion017,Fusion016]
FEATURE [Part::Box] Box010  label="Cube010"
  AttacherType = Attacher::AttachEngine3D
  Height = 0.1
  Length = 0.1
  Placement = pos=(-2,10,0) rot=(0,0.995037,0.099504;0rad)
  Width = 0.1
FEATURE [Part::MultiFuse] Fusion019
  Placement = pos=(0,10,0) rot=(1,0,0;1.5708rad)
  Shapes = -> [Box010,Fusion018]
FEATURE [Part::Box] Box011  label="Cube011"
  AttacherType = Attacher::AttachEngine3D
  Height = 0.1
  Length = 1.1
  Placement = pos=(-2,10,10) rot=(0,0.995037,0.099504;0rad)
  Width = 0.1
FEATURE [Part::MultiFuse] Fusion020
  Shapes = -> [Box011,Fusion019]
